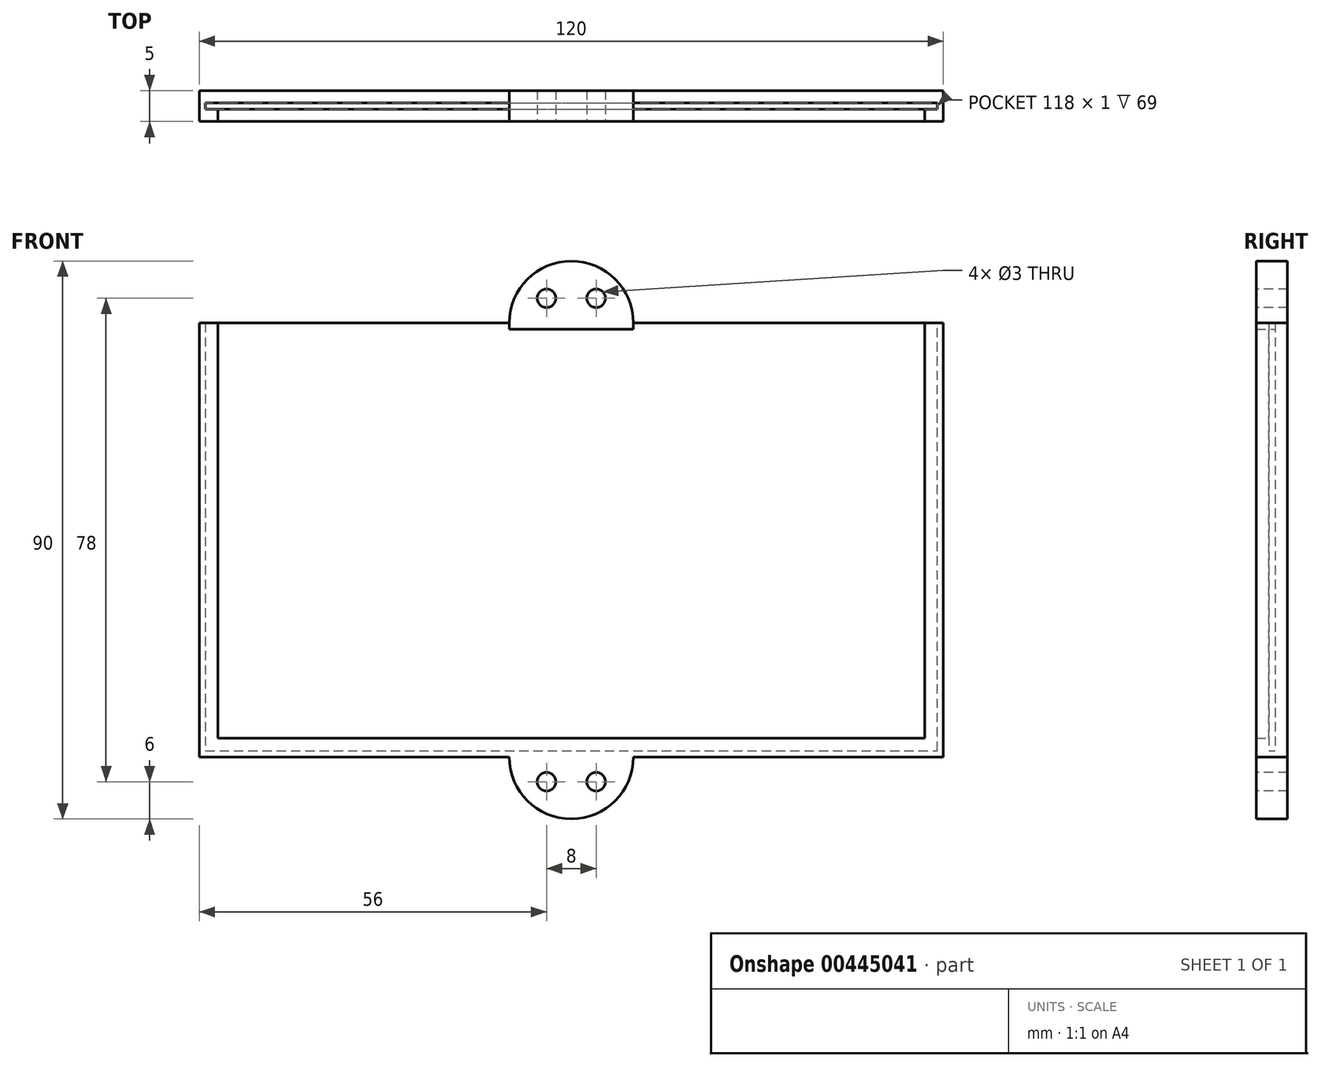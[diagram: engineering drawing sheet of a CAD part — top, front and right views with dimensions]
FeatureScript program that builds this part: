
annotation { "Feature Type Name" : "Feature", "Feature Type Description" : "" }
export const myFeature = defineFeature(function(context is Context, id is Id, definition is map)
    precondition{}
    {
        {
            var Q0;
            Q0=qCreatedBy(makeId("Front.planeOp"),FACE);
            var sketch = newSketch(context, id + "F0", { "sketchPlane" : qUnion([Q0])});
            skLineSegment(sketch, "E0.bottom", {"start": v(60, -35) * mm, "end": v(-60, -35) * mm});
            skLineSegment(sketch, "E0.top", {"start": v(60, 35) * mm, "end": v(-60, 35) * mm});
            skLineSegment(sketch, "E0.left", {"start": v(60, -35) * mm, "end": v(60, 35) * mm});
            skLineSegment(sketch, "E0.right", {"start": v(-60, -35) * mm, "end": v(-60, 35) * mm});
            skPoint(sketch, "E0.middle", {"position": v(0, 0) * mm});
            skSolve(sketch);
        }
        {
            var Q0;
            Q0 = qSketchRegion(id + "F0", true);
            extrude(context, id + "F1", {"entities" : qUnion([Q0]), "depth" : 2 * mm});
        }
        {
            var Q0;
            Q0=makeQuery(id+"F1.opExtrude","CAP_FACE",FACE,{"disambiguationData":[OSD([sQuery(id+"F0.wireOp",EDGE,"E0.bottom"),sQuery(id+"F0.wireOp",EDGE,"E0.top"),sQuery(id+"F0.wireOp",EDGE,"E0.left"),sQuery(id+"F0.wireOp",EDGE,"E0.right")])],"isStart":false});
            var sketch = newSketch(context, id + "F2", { "sketchPlane" : qUnion([Q0])});
            skPoint(sketch, "E1.endSnap0", {"position": v(0, 35) * mm});
            skLineSegment(sketch, "E2", {"start": v(-59, 35) * mm, "end": v(-59, -34) * mm});
            skLineSegment(sketch, "E3", {"start": v(-59, -34) * mm, "end": v(59, -34) * mm});
            skLineSegment(sketch, "E4", {"start": v(59, -34) * mm, "end": v(59, 35) * mm});
            skLineSegment(sketch, "E5", {"start": v(59, 35) * mm, "end": v(60, 35) * mm});
            skLineSegment(sketch, "E6", {"start": v(60, 35) * mm, "end": v(60, -35) * mm});
            skLineSegment(sketch, "E7", {"start": v(60, -35) * mm, "end": v(-60, -35) * mm});
            skLineSegment(sketch, "E8", {"start": v(-60, -35) * mm, "end": v(-60, 35) * mm});
            skLineSegment(sketch, "E9", {"start": v(-60, 35) * mm, "end": v(-59, 35) * mm});
            skSolve(sketch);
        }
        {
            var Q0;
            Q0=makeQuery(id+"F2.imprint","IMPRINT",FACE,{"disambiguationData":[TD([[makeQuery(id+"F2.imprint","IMPRINT",EDGE,{"derivedFrom":sQuery(id+"F2.wireOp",EDGE,"aRpx69pN-hMRE-y73f-m2Kp-kdF4fWzECiPd.bottom")}),1.0]])]});
            var Q1;
            Q1=makeQuery(id+"F2.imprint","IMPRINT",FACE,{"disambiguationData":[TD([[makeQuery(id+"F2.imprint","IMPRINT",EDGE,{"derivedFrom":sQuery(id+"F2.wireOp",EDGE,"E2")}),-1.0]])]});
            extrude(context, id + "F3", {"entities" : qUnion([Q0, Q1]), "operationType" : NewBodyOperationType.ADD, "depth" : 1 * mm});
        }
        {
            var Q0;
            Q0=makeQuery(id+"F3.opExtrude","CAP_FACE",FACE,{"disambiguationData":[OSD([sQuery(id+"F2.wireOp",EDGE,"E2"),sQuery(id+"F2.wireOp",EDGE,"E3"),sQuery(id+"F2.wireOp",EDGE,"E4"),sQuery(id+"F2.wireOp",EDGE,"E5"),sQuery(id+"F2.wireOp",EDGE,"E6"),sQuery(id+"F2.wireOp",EDGE,"E7"),sQuery(id+"F2.wireOp",EDGE,"E8"),sQuery(id+"F2.wireOp",EDGE,"E9")])],"isStart":false});
            var sketch = newSketch(context, id + "F4", { "sketchPlane" : qUnion([Q0])});
            skLineSegment(sketch, "E10", {"start": v(-60, 35) * mm, "end": v(-57, 35) * mm});
            skLineSegment(sketch, "E11", {"start": v(-57, 35) * mm, "end": v(-57, -32) * mm});
            skLineSegment(sketch, "E12", {"start": v(-57, -32) * mm, "end": v(57, -32) * mm});
            skLineSegment(sketch, "E13", {"start": v(57, -32) * mm, "end": v(57, 35) * mm});
            skLineSegment(sketch, "E14", {"start": v(57, 35) * mm, "end": v(60, 35) * mm});
            skLineSegment(sketch, "E15", {"start": v(60, 35) * mm, "end": v(60, -35) * mm});
            skLineSegment(sketch, "E16", {"start": v(60, -35) * mm, "end": v(-60, -35) * mm});
            skLineSegment(sketch, "E17", {"start": v(-60, -35) * mm, "end": v(-60, 35) * mm});
            skSolve(sketch);
        }
        {
            var Q0;
            Q0 = qSketchRegion(id + "F4", true);
            extrude(context, id + "F5", {"entities" : qUnion([Q0]), "operationType" : NewBodyOperationType.ADD, "depth" : 2 * mm});
        }
        {
            var Q0;
            Q0=makeQuery(id+"F1.opExtrude","CAP_FACE",FACE,{"disambiguationData":[OSD([sQuery(id+"F0.wireOp",EDGE,"E0.bottom"),sQuery(id+"F0.wireOp",EDGE,"E0.top"),sQuery(id+"F0.wireOp",EDGE,"E0.left"),sQuery(id+"F0.wireOp",EDGE,"E0.right")])],"isStart":false});
            var sketch = newSketch(context, id + "F6", { "sketchPlane" : qUnion([Q0])});
            skLineSegment(sketch, "E18.bottom", {"start": v(-10, 35) * mm, "end": v(10, 35) * mm});
            skLineSegment(sketch, "E18.top", {"start": v(-10, 34) * mm, "end": v(10, 34) * mm});
            skLineSegment(sketch, "E18.left", {"start": v(-10, 35) * mm, "end": v(-10, 34) * mm});
            skLineSegment(sketch, "E18.right", {"start": v(10, 35) * mm, "end": v(10, 34) * mm});
            skSolve(sketch);
        }
        {
            var Q0;
            Q0 = qSketchRegion(id + "F6", true);
            extrude(context, id + "F7", {"entities" : qUnion([Q0]), "operationType" : NewBodyOperationType.ADD, "depth" : 3 * mm});
        }
        {
            var Q0;
            Q0=makeQuery(id+"F7.opExtrude","CAP_FACE",FACE,{"disambiguationData":[OSD([sQuery(id+"F6.wireOp",EDGE,"E18.bottom"),sQuery(id+"F6.wireOp",EDGE,"E18.top"),sQuery(id+"F6.wireOp",EDGE,"E18.left"),sQuery(id+"F6.wireOp",EDGE,"E18.right")])],"isStart":false});
            var sketch = newSketch(context, id + "F8", { "sketchPlane" : qUnion([Q0])});
            skLineSegment(sketch, "E19.bottom", {"start": v(-10, 35) * mm, "end": v(10, 35) * mm});
            skLineSegment(sketch, "E19.top", {"start": v(0, 45) * mm, "end": v(0, 45) * mm});
            skLineSegment(sketch, "E19.left", {"start": v(-10, 35) * mm, "end": v(-10, 35) * mm});
            skLineSegment(sketch, "E19.right", {"start": v(10, 35) * mm, "end": v(10, 35) * mm});
            skPoint(sketch, "E20.visualSharp", {"position": v(-10, 45) * mm});
            skArc(sketch, "E20.filletArc", {"start": v(0, 45) * mm, "mid": v(-7.07, 42.07) * mm, "end": v(-10, 35) * mm});
            skPoint(sketch, "E21.visualSharp", {"position": v(10, 45) * mm});
            skArc(sketch, "E21.filletArc", {"start": v(10, 35) * mm, "mid": v(7.07, 42.07) * mm, "end": v(0, 45) * mm});
            skSolve(sketch);
        }
        {
            var Q0;
            Q0 = qSketchRegion(id + "F8", true);
            extrude(context, id + "F9", {"entities" : qUnion([Q0]), "operationType" : NewBodyOperationType.ADD, "oppositeDirection" : true, "depth" : 5 * mm});
        }
        {
            var Q0;
            Q0=makeQuery(id+"F5.opExtrude","CAP_FACE",FACE,{"disambiguationData":[OSD([sQuery(id+"F4.wireOp",EDGE,"E10"),sQuery(id+"F4.wireOp",EDGE,"E11"),sQuery(id+"F4.wireOp",EDGE,"E12"),sQuery(id+"F4.wireOp",EDGE,"E13"),sQuery(id+"F4.wireOp",EDGE,"E14"),sQuery(id+"F4.wireOp",EDGE,"E15"),sQuery(id+"F4.wireOp",EDGE,"E16"),sQuery(id+"F4.wireOp",EDGE,"E17")])],"isStart":false});
            var sketch = newSketch(context, id + "F10", { "sketchPlane" : qUnion([Q0])});
            skLineSegment(sketch, "E22", {"start": v(10, -35) * mm, "end": v(10, -35) * mm});
            skLineSegment(sketch, "E23", {"start": v(0, -45) * mm, "end": v(0, -45) * mm});
            skLineSegment(sketch, "E24", {"start": v(-10, -35) * mm, "end": v(-10, -35) * mm});
            skLineSegment(sketch, "E25", {"start": v(-10, -35) * mm, "end": v(10, -35) * mm});
            skPoint(sketch, "E26.visualSharp", {"position": v(10, -45) * mm});
            skArc(sketch, "E26.filletArc", {"start": v(0, -45) * mm, "mid": v(7.07, -42.07) * mm, "end": v(10, -35) * mm});
            skPoint(sketch, "E27.visualSharp", {"position": v(-10, -45) * mm});
            skArc(sketch, "E27.filletArc", {"start": v(-10, -35) * mm, "mid": v(-7.07, -42.07) * mm, "end": v(0, -45) * mm});
            skSolve(sketch);
        }
        {
            var Q0;
            Q0 = qSketchRegion(id + "F10", true);
            extrude(context, id + "F11", {"entities" : qUnion([Q0]), "operationType" : NewBodyOperationType.ADD, "oppositeDirection" : true, "depth" : 5 * mm});
        }
        {
            var Q0;
            Q0=makeQuery(id+"F9.boolean.opBoolean","MERGE",FACE,{"derivedFrom":[makeQuery(id+"F7.opExtrude","CAP_FACE",FACE,{"disambiguationData":[OSD([sQuery(id+"F6.wireOp",EDGE,"E18.bottom"),sQuery(id+"F6.wireOp",EDGE,"E18.top"),sQuery(id+"F6.wireOp",EDGE,"E18.left"),sQuery(id+"F6.wireOp",EDGE,"E18.right")])],"isStart":false}),makeQuery(id+"F9.opExtrude","CAP_FACE",FACE,{"disambiguationData":[OSD([sQuery(id+"F8.wireOp",EDGE,"E19.bottom"),sQuery(id+"F8.wireOp",EDGE,"E20.filletArc"),sQuery(id+"F8.wireOp",EDGE,"E21.filletArc")])],"isStart":true})]});
            var sketch = newSketch(context, id + "F12", { "sketchPlane" : qUnion([Q0])});
            skPoint(sketch, "E28.endSnap0", {"position": v(0, 45) * mm});
            skCircle(sketch, "E29", {"center": v(-4, -39) * mm, "radius": 1.5 * mm});
            skCircle(sketch, "E30", {"center": v(4, -39) * mm, "radius": 1.5 * mm});
            skCircle(sketch, "E31", {"center": v(-4, 39) * mm, "radius": 1.5 * mm});
            skCircle(sketch, "E32", {"center": v(4, 39) * mm, "radius": 1.5 * mm});
            skSolve(sketch);
        }
        {
            var Q0;
            Q0 = qSketchRegion(id + "F12", true);
            extrude(context, id + "F13", {"entities" : qUnion([Q0]), "operationType" : NewBodyOperationType.REMOVE, "endBound" : BoundingType.THROUGH_ALL, "oppositeDirection" : true, "depth" : 25 * mm});
        }
    });
